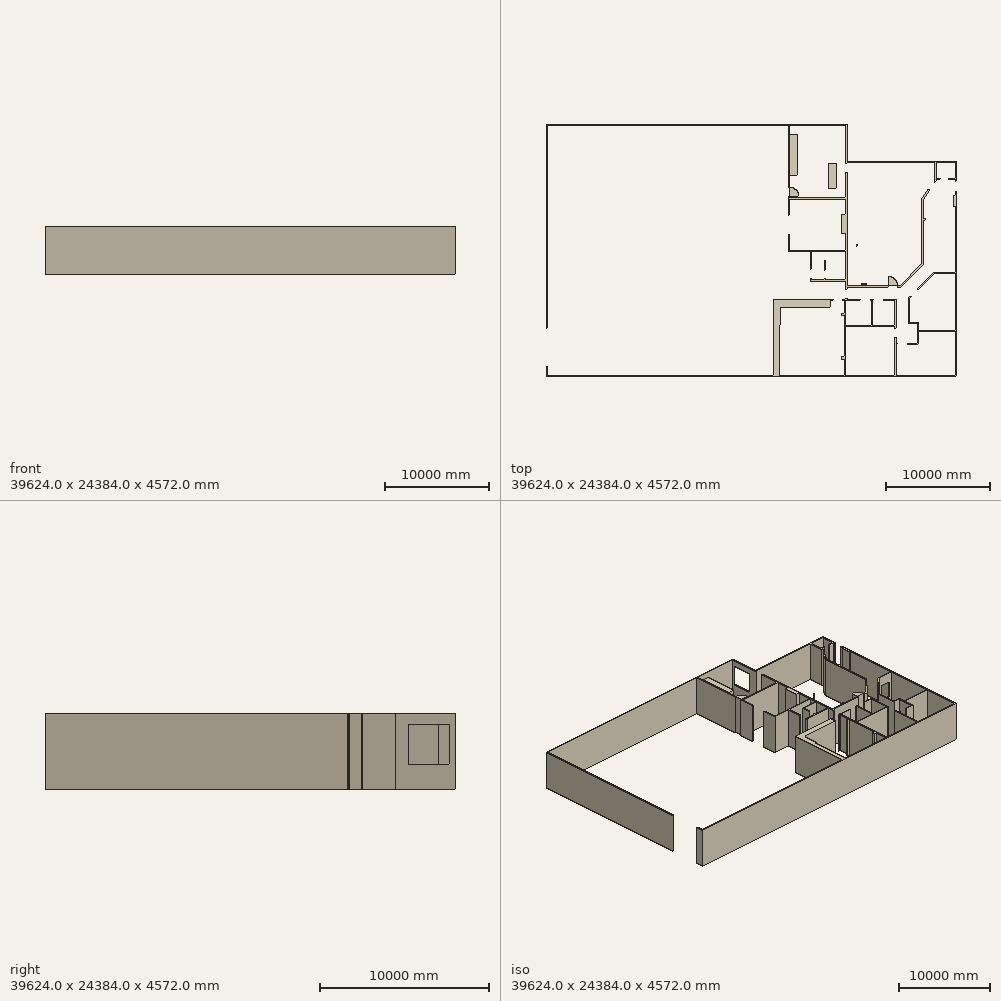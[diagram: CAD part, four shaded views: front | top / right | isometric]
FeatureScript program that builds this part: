
annotation { "Feature Type Name" : "Feature", "Feature Type Description" : "" }
export const myFeature = defineFeature(function(context is Context, id is Id, definition is map)
    precondition{}
    {
        {
            var Q0;
            Q0=qCreatedBy(makeId("Top.planeOp"),FACE);
            var sketch = newSketch(context, id + "F0", { "sketchPlane" : qUnion([Q0])});
            skLineSegment(sketch, "E0.top", {"start": v(0, 10877.8) * mm, "end": v(-10566.4, 10877.8) * mm});
            skLineSegment(sketch, "E0.left", {"start": v(0, 0) * mm, "end": v(0, 7985.1) * mm});
            skLineSegment(sketch, "E0.right", {"start": v(-10693.4, -2514.32) * mm, "end": v(-10693.4, -2412.72) * mm});
            skLineSegment(sketch, "E1.0", {"start": v(-127, 10750.8) * mm, "end": v(-1955.8, 10750.8) * mm});
            skLineSegment(sketch, "E1.1", {"start": v(-127, 127) * mm, "end": v(-127, 7985.1) * mm});
            skLineSegment(sketch, "E2", {"start": v(-1955.8, 10750.8) * mm, "end": v(-1955.8, 8979) * mm});
            skLineSegment(sketch, "E3", {"start": v(-3209.92, 7086.06) * mm, "end": v(-3209.92, 822.87) * mm});
            skLineSegment(sketch, "E4", {"start": v(-3387.72, 7139.6) * mm, "end": v(-3387.72, 895.6) * mm});
            skLineSegment(sketch, "E5.trimOffspring", {"start": v(-5415.93, -1168.4) * mm, "end": v(-5691.97, -1168.4) * mm});
            skLineSegment(sketch, "E6.trimOffspring", {"start": v(-2082.8, 10750.8) * mm, "end": v(-2082.8, 9017.25) * mm});
            skLineSegment(sketch, "E7.trimOffspring", {"start": v(-2082.8, 10750.8) * mm, "end": v(-10566.4, 10750.8) * mm});
            skLineSegment(sketch, "E8", {"start": v(-39624, -9956.8) * mm, "end": v(0, -9956.8) * mm});
            skLineSegment(sketch, "E9", {"start": v(0, 0) * mm, "end": v(0, -9956.8) * mm});
            skLineSegment(sketch, "E10.0", {"start": v(-127, 0) * mm, "end": v(-127, -9829.8) * mm});
            skLineSegment(sketch, "E10.1", {"start": v(-10820.4, -9829.8) * mm, "end": v(-127, -9829.8) * mm});
            skLineSegment(sketch, "E11", {"start": v(-39624, 14427.2) * mm, "end": v(-10566.4, 14427.2) * mm});
            skLineSegment(sketch, "E12.2", {"start": v(-39497, -9829.8) * mm, "end": v(-39497, -8992.24) * mm});
            skLineSegment(sketch, "E12.3", {"start": v(-10693.4, -9829.8) * mm, "end": v(-39497, -9829.8) * mm});
            skLineSegment(sketch, "E13", {"start": v(-10693.4, 10877.8) * mm, "end": v(-10693.4, 11212.2) * mm});
            skLineSegment(sketch, "E14", {"start": v(-10566.4, 14427.2) * mm, "end": v(-10566.4, 13955.4) * mm});
            skLineSegment(sketch, "E15", {"start": v(-39497, 14300.2) * mm, "end": v(-10693.4, 14300.2) * mm});
            skLineSegment(sketch, "E16", {"start": v(-5691.97, -1346.2) * mm, "end": v(-5691.97, -1168.4) * mm});
            skLineSegment(sketch, "E17.trimOffspring", {"start": v(-6606.37, -1168.4) * mm, "end": v(-10566.4, -1168.4) * mm});
            skLineSegment(sketch, "E18", {"start": v(-5842, -9829.8) * mm, "end": v(-5842, -6172.2) * mm});
            skLineSegment(sketch, "E19", {"start": v(-5969, -2642.3) * mm, "end": v(-5969, -5257.8) * mm});
            skLineSegment(sketch, "E20", {"start": v(-10820.4, -5156.2) * mm, "end": v(-5969, -5156.2) * mm});
            skLineSegment(sketch, "E21", {"start": v(-5969, -2642.3) * mm, "end": v(-7086.6, -2642.3) * mm});
            skLineSegment(sketch, "E22", {"start": v(-8102.6, -2642.3) * mm, "end": v(-8102.6, -5029.2) * mm});
            skLineSegment(sketch, "E23", {"start": v(-8102.6, -5029.2) * mm, "end": v(-5969, -5029.2) * mm});
            skLineSegment(sketch, "E24", {"start": v(-10820.4, -5029.2) * mm, "end": v(-8229.6, -5029.2) * mm});
            skLineSegment(sketch, "E25", {"start": v(-8229.6, -5029.2) * mm, "end": v(-8229.6, -2642.3) * mm});
            skLineSegment(sketch, "E26", {"start": v(-9245.6, -2641.6) * mm, "end": v(-9245.6, -2514.32) * mm});
            skLineSegment(sketch, "E27", {"start": v(-7086.6, -2515.3) * mm, "end": v(-7086.6, -2642.3) * mm});
            skLineSegment(sketch, "E28", {"start": v(-8001, -2642.3) * mm, "end": v(-8001, -2515.3) * mm});
            skLineSegment(sketch, "E29.trimOffspring", {"start": v(-8001, -2642.3) * mm, "end": v(-8102.6, -2642.3) * mm});
            skLineSegment(sketch, "E30.trimOffspring", {"start": v(-10566.4, 11212.2) * mm, "end": v(-10566.4, 10877.8) * mm});
            skLineSegment(sketch, "E31.trimOffspring", {"start": v(-10693.4, 13955.4) * mm, "end": v(-10693.4, 14300.2) * mm});
            skLineSegment(sketch, "E32", {"start": v(-127, 8899.5) * mm, "end": v(0, 8899.5) * mm});
            skLineSegment(sketch, "E33", {"start": v(-127, 7985.1) * mm, "end": v(0, 7985.1) * mm});
            skLineSegment(sketch, "E34.trimOffspring", {"start": v(-127, 8899.5) * mm, "end": v(-127, 10750.8) * mm});
            skLineSegment(sketch, "E35.trimOffspring", {"start": v(0, 8899.5) * mm, "end": v(0, 10877.8) * mm});
            skLineSegment(sketch, "E36", {"start": v(-5969, -5257.8) * mm, "end": v(-5842, -5257.8) * mm});
            skLineSegment(sketch, "E37", {"start": v(-5969, -6172.2) * mm, "end": v(-5842, -6172.2) * mm});
            skLineSegment(sketch, "E38.trimOffspring", {"start": v(-5969, -6172.2) * mm, "end": v(-5969, -9829.8) * mm});
            skLineSegment(sketch, "E39.trimOffspring", {"start": v(-5842, -5257.8) * mm, "end": v(-5842, -2515.3) * mm});
            skLineSegment(sketch, "E40", {"start": v(-127, -5486.4) * mm, "end": v(-3683, -5486.4) * mm});
            skLineSegment(sketch, "E41", {"start": v(-3683, -5613.4) * mm, "end": v(-127, -5613.4) * mm});
            skLineSegment(sketch, "E42", {"start": v(-14122.4, 401.43) * mm, "end": v(-13995.4, 401.43) * mm});
            skLineSegment(sketch, "E43", {"start": v(-13995.4, 401.43) * mm, "end": v(-13995.4, 2103.23) * mm});
            skLineSegment(sketch, "E44", {"start": v(-14122.4, -512.97) * mm, "end": v(-14122.4, -741.57) * mm});
            skLineSegment(sketch, "E45", {"start": v(-14122.4, -741.57) * mm, "end": v(-10693.4, -741.57) * mm});
            skLineSegment(sketch, "E46", {"start": v(-13995.4, -614.57) * mm, "end": v(-13995.4, -512.97) * mm});
            skLineSegment(sketch, "E47", {"start": v(-13995.4, -512.97) * mm, "end": v(-14122.4, -512.97) * mm});
            skLineSegment(sketch, "E48.trimOffspring", {"start": v(-10693.4, -614.57) * mm, "end": v(-10693.4, 2103.23) * mm});
            skLineSegment(sketch, "E49", {"start": v(-17602.2, -2641.6) * mm, "end": v(-11913.18, -2641.6) * mm});
            skLineSegment(sketch, "E50", {"start": v(-17729.2, -2514.6) * mm, "end": v(-17729.2, -9829.8) * mm});
            skLineSegment(sketch, "E51", {"start": v(-17602.2, -2641.6) * mm, "end": v(-17602.2, -9829.8) * mm});
            skLineSegment(sketch, "E52", {"start": v(-7086.6, -2515.3) * mm, "end": v(-5842, -2515.3) * mm});
            skLineSegment(sketch, "E53.trimOffspring", {"start": v(-10820.4, -2641.6) * mm, "end": v(-10820.4, -9829.8) * mm});
            skLineSegment(sketch, "E54", {"start": v(-13995.4, -614.57) * mm, "end": v(-10693.4, -614.57) * mm});
            skLineSegment(sketch, "E55", {"start": v(-13995.4, 2103.23) * mm, "end": v(-10693.4, 2103.23) * mm});
            skLineSegment(sketch, "E56.trimOffspring", {"start": v(-10693.4, 2230.23) * mm, "end": v(-10693.4, 9734.8) * mm});
            skLineSegment(sketch, "E57.trimOffspring", {"start": v(-5341.37, -1346.2) * mm, "end": v(-5691.97, -1346.2) * mm});
            skLineSegment(sketch, "E58", {"start": v(-39624, -8992.24) * mm, "end": v(-39497, -8992.24) * mm});
            skLineSegment(sketch, "E59", {"start": v(-39624, -5334.64) * mm, "end": v(-39497, -5334.64) * mm});
            skLineSegment(sketch, "E60.trimOffspring", {"start": v(-39497, -5334.64) * mm, "end": v(-39497, 14300.2) * mm});
            skLineSegment(sketch, "E61.trimOffspring", {"start": v(-39624, -5334.64) * mm, "end": v(-39624, 14427.2) * mm});
            skLineSegment(sketch, "E62", {"start": v(-10693.4, 10649.2) * mm, "end": v(-10566.4, 10649.2) * mm});
            skLineSegment(sketch, "E63", {"start": v(-10693.4, 9734.8) * mm, "end": v(-10566.4, 9734.8) * mm});
            skLineSegment(sketch, "E64.trimOffspring", {"start": v(-10693.4, 10649.2) * mm, "end": v(-10693.4, 10877.8) * mm});
            skLineSegment(sketch, "E65.trimOffspring", {"start": v(-10566.4, 10649.2) * mm, "end": v(-10566.4, 10750.8) * mm});
            skLineSegment(sketch, "E66", {"start": v(-10566.4, -1168.4) * mm, "end": v(-10566.4, 9734.8) * mm});
            skLineSegment(sketch, "E67", {"start": v(-10998.78, -2641.6) * mm, "end": v(-10998.78, -2514.32) * mm});
            skLineSegment(sketch, "E68", {"start": v(-11913.18, -2641.6) * mm, "end": v(-11913.18, -2514.6) * mm});
            skLineSegment(sketch, "E69.trimOffspring", {"start": v(-11913.18, -2514.6) * mm, "end": v(-17729.2, -2514.6) * mm});
            skLineSegment(sketch, "E70", {"start": v(-4495.8, -4716.3) * mm, "end": v(-4495.8, -2406.4) * mm});
            skLineSegment(sketch, "E71", {"start": v(-1955.8, 9226.8) * mm, "end": v(-1498.6, 9226.8) * mm});
            skLineSegment(sketch, "E72", {"start": v(-1498.6, 9226.8) * mm, "end": v(-1498.6, 9099.8) * mm});
            skLineSegment(sketch, "E73", {"start": v(-1955.8, 9099.8) * mm, "end": v(-1498.6, 9099.8) * mm});
            skLineSegment(sketch, "E74", {"start": v(-127, 9226.8) * mm, "end": v(-736.6, 9226.8) * mm});
            skLineSegment(sketch, "E75", {"start": v(-736.6, 9226.8) * mm, "end": v(-736.6, 9099.8) * mm});
            skLineSegment(sketch, "E76", {"start": v(-736.6, 9099.8) * mm, "end": v(-127, 9099.8) * mm});
            skLineSegment(sketch, "E77", {"start": v(-16141.7, 7334.25) * mm, "end": v(-10693.4, 7334.25) * mm});
            skLineSegment(sketch, "E78", {"start": v(-10693.4, 7207.25) * mm, "end": v(-16141.7, 7207.25) * mm});
            skLineSegment(sketch, "E79", {"start": v(-10693.4, 5686.16) * mm, "end": v(-11121.45, 5686.16) * mm});
            skLineSegment(sketch, "E80", {"start": v(-11121.45, 5686.16) * mm, "end": v(-11121.45, 3915.17) * mm});
            skLineSegment(sketch, "E81", {"start": v(-11121.45, 3915.17) * mm, "end": v(-10693.4, 3915.17) * mm});
            skLineSegment(sketch, "E82", {"start": v(-10693.4, -2641.6) * mm, "end": v(-10693.4, -9829.8) * mm});
            skLineSegment(sketch, "E83", {"start": v(-39624, -9956.8) * mm, "end": v(-39624, -8992.24) * mm});
            skLineSegment(sketch, "E84", {"start": v(-4495.8, -2406.4) * mm, "end": v(-4328.22, -2235.85) * mm});
            skLineSegment(sketch, "E85", {"start": v(-4622.8, -2354.44) * mm, "end": v(-4418.8, -2146.84) * mm});
            skLineSegment(sketch, "E86", {"start": v(-5415.93, -1168.4) * mm, "end": v(-3387.72, 895.6) * mm});
            skLineSegment(sketch, "E87", {"start": v(-5341.37, -1346.2) * mm, "end": v(-3209.92, 822.87) * mm});
            skLineSegment(sketch, "E88", {"start": v(-6606.37, -1168.4) * mm, "end": v(-6606.37, -254) * mm});
            skArc(sketch, "E89", {"start": v(-5691.97, -1168.4) * mm, "mid": v(-5959.8, -521.82) * mm, "end": v(-6606.37, -254) * mm});
            skLineSegment(sketch, "E90", {"start": v(-6606.37, -1168.4) * mm, "end": v(-5691.97, -1168.4) * mm});
            skLineSegment(sketch, "E91", {"start": v(-2131.14, 0) * mm, "end": v(-127, 0) * mm});
            skLineSegment(sketch, "E92", {"start": v(-2184.4, 127) * mm, "end": v(-127, 127) * mm});
            skLineSegment(sketch, "E93", {"start": v(-6606.37, -1168.4) * mm, "end": v(-6606.37, -1295.4) * mm});
            skLineSegment(sketch, "E94", {"start": v(-6606.37, -1295.4) * mm, "end": v(-10566.4, -1295.4) * mm});
            skLineSegment(sketch, "E95", {"start": v(-10566.4, -2514.32) * mm, "end": v(-10566.4, -2412.72) * mm});
            skLineSegment(sketch, "E96", {"start": v(-4622.8, -2354.44) * mm, "end": v(-4622.8, -4843.3) * mm});
            skLineSegment(sketch, "E97", {"start": v(-3209.92, 7086.06) * mm, "end": v(-2573.14, 8047.2) * mm});
            skLineSegment(sketch, "E98", {"start": v(-2721.37, 8145.4) * mm, "end": v(-2573.14, 8047.2) * mm});
            skLineSegment(sketch, "E99", {"start": v(-2173.99, 8879.62) * mm, "end": v(-2068.11, 8809.48) * mm});
            skLineSegment(sketch, "E100.trimOffspring", {"start": v(-2721.37, 8145.4) * mm, "end": v(-3387.72, 7139.6) * mm});
            skLineSegment(sketch, "E101.trimOffspring", {"start": v(-2068.11, 8809.48) * mm, "end": v(-1955.8, 8979) * mm});
            skLineSegment(sketch, "E102", {"start": v(-2173.99, 8879.62) * mm, "end": v(-2082.8, 9017.25) * mm});
            skLineSegment(sketch, "E103", {"start": v(0, 123.6) * mm, "end": v(326.15, 123.6) * mm});
            skLineSegment(sketch, "E104", {"start": v(0, 936.4) * mm, "end": v(323.16, 936.4) * mm});
            skLineSegment(sketch, "E105", {"start": v(-9144, -1131.86) * mm, "end": v(-9144, -928.66) * mm});
            skLineSegment(sketch, "E106", {"start": v(-9144, -928.66) * mm, "end": v(-9093.2, -928.66) * mm});
            skLineSegment(sketch, "E107", {"start": v(-9093.2, -928.66) * mm, "end": v(-9093.2, -999.03) * mm});
            skLineSegment(sketch, "E108", {"start": v(-9093.2, -999.03) * mm, "end": v(-8788.4, -999.03) * mm});
            skLineSegment(sketch, "E109", {"start": v(-8788.4, -999.03) * mm, "end": v(-8788.4, -928.66) * mm});
            skLineSegment(sketch, "E110", {"start": v(-8788.4, -928.66) * mm, "end": v(-8737.6, -928.66) * mm});
            skLineSegment(sketch, "E111", {"start": v(-8737.6, -928.66) * mm, "end": v(-8737.6, -1131.86) * mm});
            skLineSegment(sketch, "E112", {"start": v(-9093.2, -1131.86) * mm, "end": v(-9093.2, -1049.83) * mm});
            skLineSegment(sketch, "E113", {"start": v(-9093.2, -1049.83) * mm, "end": v(-8788.4, -1049.83) * mm});
            skLineSegment(sketch, "E114", {"start": v(-8788.4, -1049.83) * mm, "end": v(-8788.4, -1131.86) * mm});
            skLineSegment(sketch, "E115", {"start": v(-9144, -1131.86) * mm, "end": v(-9093.2, -1131.86) * mm});
            skLineSegment(sketch, "E116", {"start": v(-8788.4, -1131.86) * mm, "end": v(-8737.6, -1131.86) * mm});
            skLineSegment(sketch, "E117", {"start": v(-4418.8, -2146.84) * mm, "end": v(-4328.22, -2235.85) * mm});
            skLineSegment(sketch, "E118", {"start": v(-3687.32, -1583.64) * mm, "end": v(-3777.9, -1494.63) * mm});
            skLineSegment(sketch, "E119.trimOffspring", {"start": v(-3777.9, -1494.63) * mm, "end": v(-2184.4, 127) * mm});
            skLineSegment(sketch, "E120.trimOffspring", {"start": v(-3687.32, -1583.64) * mm, "end": v(-2131.14, 0) * mm});
            skLineSegment(sketch, "E121", {"start": v(-16141.7, 2230.23) * mm, "end": v(-16141.7, 3829.05) * mm});
            skLineSegment(sketch, "E122", {"start": v(-14122.4, 2103.23) * mm, "end": v(-16268.7, 2103.23) * mm});
            skLineSegment(sketch, "E123", {"start": v(-16268.7, 2103.23) * mm, "end": v(-16268.7, 3829.05) * mm});
            skLineSegment(sketch, "E124", {"start": v(-16268.7, 5657.85) * mm, "end": v(-16141.7, 5657.85) * mm});
            skLineSegment(sketch, "E125", {"start": v(-16268.7, 3829.05) * mm, "end": v(-16141.7, 3829.05) * mm});
            skLineSegment(sketch, "E126.trimOffspring", {"start": v(-16268.7, 5657.85) * mm, "end": v(-16268.7, 7435.85) * mm});
            skLineSegment(sketch, "E127.trimOffspring", {"start": v(-16141.7, 5657.85) * mm, "end": v(-16141.7, 7435.85) * mm});
            skLineSegment(sketch, "E128", {"start": v(-10693.4, 13955.4) * mm, "end": v(-10693.4, 11212.2) * mm});
            skLineSegment(sketch, "E129", {"start": v(-10566.4, 13955.4) * mm, "end": v(-10566.4, 11212.2) * mm});
            skLineSegment(sketch, "E130", {"start": v(-16268.7, 7435.85) * mm, "end": v(-16141.7, 7435.85) * mm});
            skLineSegment(sketch, "E131", {"start": v(-16268.7, 8350.25) * mm, "end": v(-16141.7, 8350.25) * mm});
            skLineSegment(sketch, "E132.trimOffspring", {"start": v(-16268.7, 8350.25) * mm, "end": v(-16268.7, 14300.2) * mm});
            skLineSegment(sketch, "E133.trimOffspring", {"start": v(-16141.7, 8350.25) * mm, "end": v(-16141.7, 14300.2) * mm});
            skLineSegment(sketch, "E134", {"start": v(-16141.7, 7435.85) * mm, "end": v(-15227.3, 7435.85) * mm});
            skArc(sketch, "E135", {"start": v(-15227.3, 7435.85) * mm, "mid": v(-15495.12, 8082.43) * mm, "end": v(-16141.7, 8350.25) * mm});
            skLineSegment(sketch, "E136", {"start": v(-16141.7, 8350.25) * mm, "end": v(-16141.7, 7435.85) * mm});
            skLineSegment(sketch, "E137", {"start": v(-16101.24, 13428.33) * mm, "end": v(-15339.24, 13428.33) * mm});
            skLineSegment(sketch, "E138", {"start": v(-15339.24, 13428.33) * mm, "end": v(-15339.24, 11904.33) * mm});
            skLineSegment(sketch, "E139", {"start": v(-15339.24, 11904.33) * mm, "end": v(-16101.24, 11904.33) * mm});
            skLineSegment(sketch, "E140", {"start": v(-15339.24, 11904.33) * mm, "end": v(-15339.24, 9465.93) * mm});
            skLineSegment(sketch, "E141", {"start": v(-8229.6, -2642.3) * mm, "end": v(-8331.2, -2642.3) * mm});
            skLineSegment(sketch, "E142", {"start": v(-8331.2, -2642.3) * mm, "end": v(-8331.2, -2515.3) * mm});
            skLineSegment(sketch, "E143", {"start": v(-3683, -4716.3) * mm, "end": v(-3683, -6875.3) * mm});
            skLineSegment(sketch, "E144", {"start": v(-3683, -6875.3) * mm, "end": v(-4746.92, -6875.3) * mm});
            skLineSegment(sketch, "E145", {"start": v(-5842, -6748.3) * mm, "end": v(-5661.32, -6748.3) * mm});
            skLineSegment(sketch, "E146", {"start": v(-3810, -6748.3) * mm, "end": v(-3810, -4843.3) * mm});
            skLineSegment(sketch, "E147", {"start": v(-4495.8, -4716.3) * mm, "end": v(-3683, -4716.3) * mm});
            skLineSegment(sketch, "E148", {"start": v(-4622.8, -4843.3) * mm, "end": v(-3810, -4843.3) * mm});
            skLineSegment(sketch, "E149", {"start": v(-5661.32, -6875.3) * mm, "end": v(-5661.32, -6748.3) * mm});
            skLineSegment(sketch, "E150", {"start": v(-4746.92, -6875.3) * mm, "end": v(-4746.92, -6748.3) * mm});
            skLineSegment(sketch, "E151.trimOffspring", {"start": v(-5661.32, -6875.3) * mm, "end": v(-5842, -6875.3) * mm});
            skLineSegment(sketch, "E152.trimOffspring", {"start": v(-4746.92, -6748.3) * mm, "end": v(-3810, -6748.3) * mm});
            skLineSegment(sketch, "E153", {"start": v(-14122.4, 2103.23) * mm, "end": v(-14122.4, 401.43) * mm});
            skLineSegment(sketch, "E154", {"start": v(-16141.7, 2230.23) * mm, "end": v(-10693.4, 2230.23) * mm});
            skLineSegment(sketch, "E155", {"start": v(-8331.2, -2515.3) * mm, "end": v(-8001, -2515.3) * mm});
            skLineSegment(sketch, "E156", {"start": v(-10693.4, -1498.32) * mm, "end": v(-10566.4, -1498.32) * mm});
            skLineSegment(sketch, "E157", {"start": v(-10693.4, -2412.72) * mm, "end": v(-10566.4, -2412.72) * mm});
            skLineSegment(sketch, "E158.trimOffspring", {"start": v(-10693.4, -1498.32) * mm, "end": v(-10693.4, -741.57) * mm});
            skLineSegment(sketch, "E159.trimOffspring", {"start": v(-10566.4, -1498.32) * mm, "end": v(-10566.4, -1295.4) * mm});
            skLineSegment(sketch, "E160", {"start": v(-16101.24, 11904.33) * mm, "end": v(-16101.24, 13428.33) * mm});
            skLineSegment(sketch, "E161", {"start": v(-16101.24, 11904.33) * mm, "end": v(-16101.24, 9465.93) * mm});
            skLineSegment(sketch, "E162", {"start": v(-15339.24, 9465.93) * mm, "end": v(-16101.24, 9465.93) * mm});
            skLineSegment(sketch, "E163", {"start": v(-10693.4, -2641.6) * mm, "end": v(-9245.6, -2641.6) * mm});
            skLineSegment(sketch, "E164", {"start": v(-10998.78, -2641.6) * mm, "end": v(-10820.4, -2641.6) * mm});
            skLineSegment(sketch, "E165", {"start": v(-10998.78, -2514.32) * mm, "end": v(-10693.4, -2514.32) * mm});
            skLineSegment(sketch, "E166", {"start": v(-10566.4, -2514.32) * mm, "end": v(-9245.6, -2514.32) * mm});
            skLineSegment(sketch, "E167", {"start": v(-12725.4, -614.57) * mm, "end": v(-12725.4, -424.07) * mm});
            skLineSegment(sketch, "E168", {"start": v(-12725.4, 1290.43) * mm, "end": v(-10693.4, 1290.43) * mm});
            skLineSegment(sketch, "E169", {"start": v(-10693.4, 13955.4) * mm, "end": v(-10566.4, 13955.4) * mm});
            skLineSegment(sketch, "E170", {"start": v(-10693.4, 11212.2) * mm, "end": v(-10566.4, 11212.2) * mm});
            skLineSegment(sketch, "E171", {"start": v(-127, 7534.25) * mm, "end": v(-292.1, 7534.25) * mm});
            skLineSegment(sketch, "E172", {"start": v(-292.1, 7534.25) * mm, "end": v(-292.1, 6530.95) * mm});
            skLineSegment(sketch, "E173", {"start": v(-292.1, 6530.95) * mm, "end": v(-127, 6530.95) * mm});
            skLineSegment(sketch, "E174", {"start": v(-1481.72, 0) * mm, "end": v(-1481.72, 127) * mm});
            skLineSegment(sketch, "E175", {"start": v(-554.77, 0) * mm, "end": v(-554.77, 127) * mm});
            skLineSegment(sketch, "E176", {"start": v(-10820.4, -7975.6) * mm, "end": v(-11125.2, -7975.6) * mm});
            skLineSegment(sketch, "E177", {"start": v(-11125.2, -7975.6) * mm, "end": v(-11125.2, -8318.5) * mm});
            skLineSegment(sketch, "E178", {"start": v(-11125.2, -8318.5) * mm, "end": v(-10820.4, -8318.5) * mm});
            skLineSegment(sketch, "E179", {"start": v(-10693.4, 1239.63) * mm, "end": v(-12674.6, 1239.63) * mm});
            skLineSegment(sketch, "E180", {"start": v(-12674.6, 1239.63) * mm, "end": v(-12674.6, 337.93) * mm});
            skLineSegment(sketch, "E181", {"start": v(-12725.4, 337.93) * mm, "end": v(-12674.6, 337.93) * mm});
            skLineSegment(sketch, "E182", {"start": v(-12725.4, -424.07) * mm, "end": v(-12674.6, -424.07) * mm});
            skLineSegment(sketch, "E183.trimOffspring", {"start": v(-12674.6, -424.07) * mm, "end": v(-12674.6, -614.57) * mm});
            skLineSegment(sketch, "E184.trimOffspring", {"start": v(-12725.4, 337.93) * mm, "end": v(-12725.4, 1290.43) * mm});
            skLineSegment(sketch, "E185.bottom", {"start": v(-9664.43, 2774) * mm, "end": v(-9537.43, 2774) * mm});
            skLineSegment(sketch, "E185.top", {"start": v(-9664.43, 2647) * mm, "end": v(-9537.43, 2647) * mm});
            skLineSegment(sketch, "E185.left", {"start": v(-9664.43, 2774) * mm, "end": v(-9664.43, 2647) * mm});
            skLineSegment(sketch, "E185.right", {"start": v(-9537.43, 2774) * mm, "end": v(-9537.43, 2647) * mm});
            skLineSegment(sketch, "E186", {"start": v(-3209.92, 5104.86) * mm, "end": v(-2981.32, 5104.86) * mm});
            skLineSegment(sketch, "E187", {"start": v(-2981.32, 5358.86) * mm, "end": v(-2981.32, 5104.86) * mm});
            skLineSegment(sketch, "E188", {"start": v(-2981.32, 5358.86) * mm, "end": v(-3209.92, 5358.86) * mm});
            skLineSegment(sketch, "E189", {"start": v(-10820.4, -3835.4) * mm, "end": v(-11125.2, -3835.4) * mm});
            skLineSegment(sketch, "E190", {"start": v(-11125.2, -3835.4) * mm, "end": v(-11125.2, -4064) * mm});
            skLineSegment(sketch, "E191", {"start": v(-11125.2, -4064) * mm, "end": v(-10820.4, -4064) * mm});
            skLineSegment(sketch, "E192", {"start": v(-12166.6, -2641.6) * mm, "end": v(-12166.6, -3251.2) * mm});
            skLineSegment(sketch, "E193", {"start": v(-12166.6, -3251.2) * mm, "end": v(-16992.6, -3251.2) * mm});
            skLineSegment(sketch, "E194", {"start": v(-16992.6, -3251.2) * mm, "end": v(-16992.6, -5041.9) * mm});
            skLineSegment(sketch, "E195", {"start": v(-16992.6, -5041.9) * mm, "end": v(-17602.2, -5041.9) * mm});
            skLineSegment(sketch, "E196", {"start": v(-17145, -5041.9) * mm, "end": v(-17145, -9829.8) * mm});
            skLineSegment(sketch, "E197", {"start": v(-10566.4, 6010.4) * mm, "end": v(-10515.6, 6010.4) * mm});
            skLineSegment(sketch, "E198", {"start": v(-10566.4, 4791.2) * mm, "end": v(-9767.8, 4791.2) * mm});
            skLineSegment(sketch, "E199", {"start": v(-10566.4, 3572) * mm, "end": v(-10515.6, 3572) * mm});
            skLineSegment(sketch, "E200", {"start": v(-10566.4, 8095.74) * mm, "end": v(-10515.6, 8095.74) * mm});
            skLineSegment(sketch, "E201", {"start": v(-10566.4, 1486.66) * mm, "end": v(-10515.6, 1486.66) * mm});
            skLineSegment(sketch, "E202", {"start": v(-10515.6, 3572) * mm, "end": v(-10515.6, 6010.4) * mm});
            skLineSegment(sketch, "E203", {"start": v(-10515.6, 6010.4) * mm, "end": v(-10515.6, 8095.74) * mm});
            skLineSegment(sketch, "E204", {"start": v(-10515.6, 3572) * mm, "end": v(-10515.6, 1486.66) * mm});
            skSolve(sketch);
        }
        {
            var Q0;
            Q0 = qSketchRegion(id + "F0", true);
            extrude(context, id + "F1", {"entities" : qUnion([Q0]), "depth" : 4572 * mm, "offsetDistance" : 25.4 * mm});
        }
        {
            var Q0;
            Q0=qCreatedBy(makeId("Top.planeOp"),FACE);
            var sketch = newSketch(context, id + "F2", { "sketchPlane" : qUnion([Q0])});
            skLineSegment(sketch, "E205", {"start": v(-12369.8, 10687.05) * mm, "end": v(-12369.8, 8248.65) * mm});
            skLineSegment(sketch, "E206", {"start": v(-12369.8, 8248.65) * mm, "end": v(-11607.8, 8248.65) * mm});
            skLineSegment(sketch, "E207", {"start": v(-11607.8, 8248.65) * mm, "end": v(-11607.8, 10687.05) * mm});
            skLineSegment(sketch, "E208", {"start": v(-11607.8, 10687.05) * mm, "end": v(-12369.8, 10687.05) * mm});
            skSolve(sketch);
        }
        {
            var Q0;
            Q0 = qSketchRegion(id + "F2", true);
            extrude(context, id + "F3", {"entities" : qUnion([Q0]), "depth" : 1524 * mm, "offsetDistance" : 25.4 * mm});
        }
        {
            var Q0;
            Q0=makeQuery(id+"F1.opExtrude","SWEPT_FACE",FACE,{"disambiguationData":[OSD([sQuery(id+"F0.wireOp",EDGE,"E14"),sQuery(id+"F0.wireOp",EDGE,"E30.trimOffspring"),sQuery(id+"F0.wireOp",EDGE,"E129")])]});
            var sketch = newSketch(context, id + "F4", { "sketchPlane" : qUnion([Q0])});
            skLineSegment(sketch, "E209.bottom", {"start": v(11619.1, 3889.5) * mm, "end": v(14057.5, 3889.5) * mm});
            skLineSegment(sketch, "E209.top", {"start": v(11619.1, 1517) * mm, "end": v(14057.5, 1517) * mm});
            skLineSegment(sketch, "E209.left", {"start": v(11619.1, 3889.5) * mm, "end": v(11619.1, 1517) * mm});
            skLineSegment(sketch, "E209.right", {"start": v(14057.5, 3889.5) * mm, "end": v(14057.5, 1517) * mm});
            skSolve(sketch);
        }
        {
            var Q0;
            Q0=makeQuery(id+"F4.imprint","IMPRINT",FACE,{"disambiguationData":[TD([[makeQuery(id+"F4.imprint","IMPRINT",EDGE,{"derivedFrom":sQuery(id+"F4.wireOp",EDGE,"E209.bottom")}),-1.0]])]});
            extrude(context, id + "F5", {"entities" : qUnion([Q0]), "operationType" : NewBodyOperationType.REMOVE, "oppositeDirection" : true, "depth" : 127 * mm, "offsetDistance" : 25.4 * mm});
        }
        {
            var Q0;
            Q0=makeQuery(id+"F1.opExtrude","SWEPT_FACE",FACE,{"disambiguationData":[OSD([sQuery(id+"F0.wireOp",EDGE,"E92")])]});
            var sketch = newSketch(context, id + "F6", { "sketchPlane" : qUnion([Q0])});
            skLineSegment(sketch, "E210.bottom", {"start": v(559.63, 3421.7) * mm, "end": v(1778.83, 3421.7) * mm});
            skLineSegment(sketch, "E210.top", {"start": v(559.63, 1566.08) * mm, "end": v(1778.83, 1566.08) * mm});
            skLineSegment(sketch, "E210.left", {"start": v(559.63, 3421.7) * mm, "end": v(559.63, 1566.08) * mm});
            skLineSegment(sketch, "E210.right", {"start": v(1778.83, 3421.7) * mm, "end": v(1778.83, 1566.08) * mm});
            skSolve(sketch);
        }
        {
            var Q0;
            Q0 = qSketchRegion(id + "F6", true);
            extrude(context, id + "F7", {"entities" : qUnion([Q0]), "operationType" : NewBodyOperationType.REMOVE, "oppositeDirection" : true, "depth" : 127 * mm, "offsetDistance" : 25.4 * mm});
        }
    });
